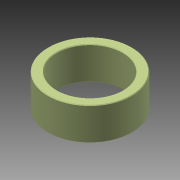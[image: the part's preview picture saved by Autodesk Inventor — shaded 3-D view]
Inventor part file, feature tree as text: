
AUTODESK INVENTOR PART (.ipt)
format: ipt  version: 2015 (Build 190159000, 159)  size: 91,648 bytes
history: native  units: mm
features: extrude x1, chamfer x1, sketch x1
ambient origin geometry x8: Origin, YZ Plane, XZ Plane, XY Plane, X Axis, Y Axis, Z Axis, Center Point
bodies: Body1 (feature_tree)
feature tree (3):
  extrude  "拉伸2"  Depth=25.0mm
  chamfer  "倒角1"  Distance=25.0mm
  sketch  "草图2"  dims[d4=64.0mm d5=50.0mm d6=25.0mm d7=0.0mm d8=0.5mm d9=2.0mm d10=45.0deg]
